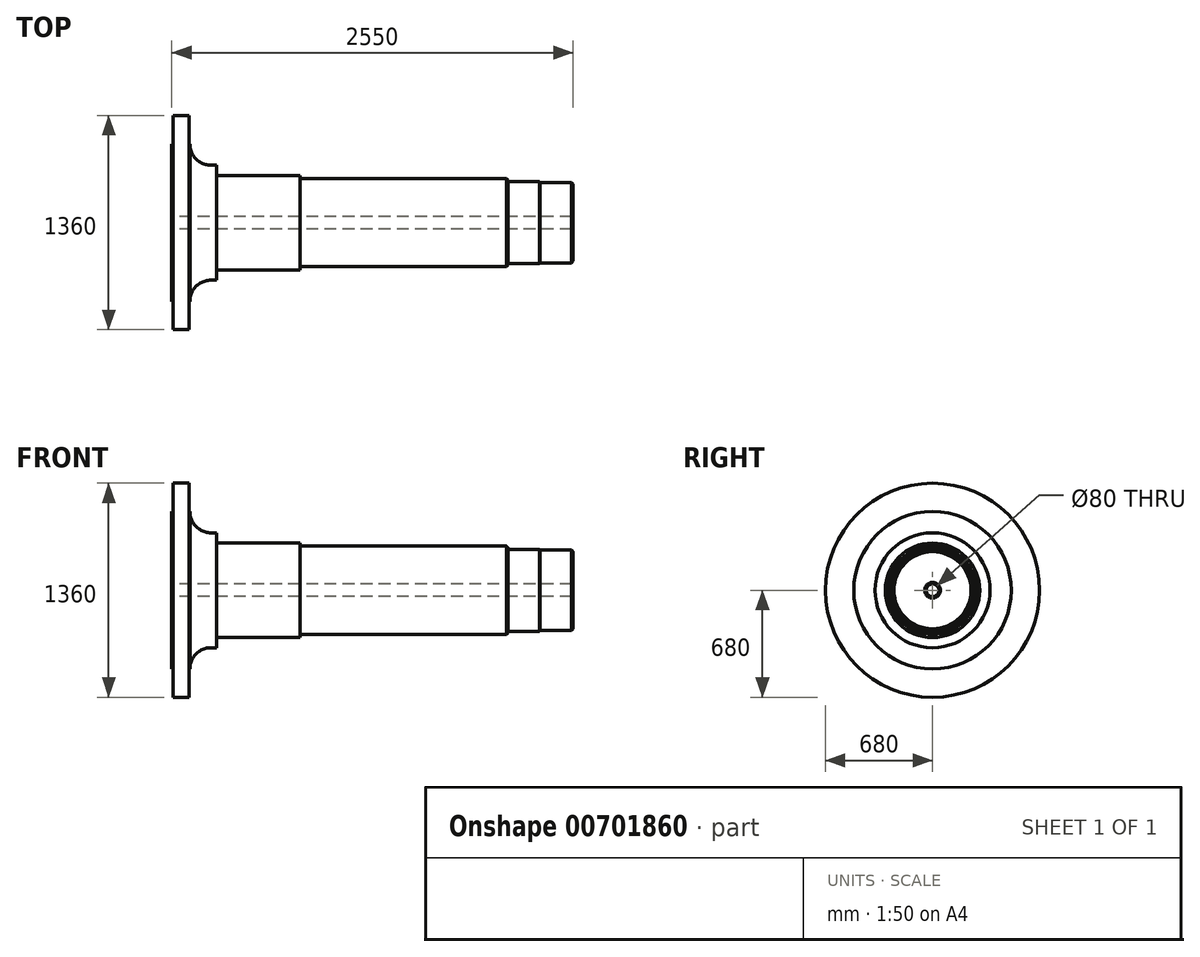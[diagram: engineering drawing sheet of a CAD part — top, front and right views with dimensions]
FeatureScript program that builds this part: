
annotation { "Feature Type Name" : "Feature", "Feature Type Description" : "" }
export const myFeature = defineFeature(function(context is Context, id is Id, definition is map)
    precondition{}
    {
        {
            var Q0;
            Q0=qCreatedBy(makeId("Front.planeOp"),FACE);
            var sketch = newSketch(context, id + "F0", { "sketchPlane" : qUnion([Q0])});
            skLineSegment(sketch, "E0", {"start": v(10, 40) * mm, "end": v(0, 50) * mm});
            skLineSegment(sketch, "E1", {"start": v(0, 50) * mm, "end": v(0, 500) * mm});
            skLineSegment(sketch, "E2", {"start": v(0, 500) * mm, "end": v(10, 500) * mm});
            skLineSegment(sketch, "E3", {"start": v(10, 500) * mm, "end": v(10, 680) * mm});
            skLineSegment(sketch, "E4", {"start": v(10, 680) * mm, "end": v(110, 680) * mm});
            skLineSegment(sketch, "E5", {"start": v(110, 680) * mm, "end": v(110, 500) * mm});
            skLineSegment(sketch, "E6", {"start": v(110, 500) * mm, "end": v(115, 500) * mm});
            skArc(sketch, "E7", {"start": v(115, 500) * mm, "mid": v(154.54, 404.54) * mm, "end": v(250, 365) * mm});
            skLineSegment(sketch, "E8", {"start": v(250, 365) * mm, "end": v(285, 365) * mm});
            skLineSegment(sketch, "E9", {"start": v(285, 365) * mm, "end": v(285, 300) * mm});
            skLineSegment(sketch, "E10", {"start": v(285, 300) * mm, "end": v(815, 300) * mm});
            skLineSegment(sketch, "E11", {"start": v(815, 300) * mm, "end": v(815, 280) * mm});
            skLineSegment(sketch, "E12", {"start": v(2550, 245) * mm, "end": v(2550, 50) * mm});
            skLineSegment(sketch, "E13", {"start": v(2550, 50) * mm, "end": v(2540, 40) * mm});
            skLineSegment(sketch, "E14", {"start": v(2540, 40) * mm, "end": v(10, 40) * mm});
            skLineSegment(sketch, "E15", {"start": v(0, 0) * mm, "end": v(2550, 0) * mm, "construction": true});
            skLineSegment(sketch, "E16", {"start": v(115, 500) * mm, "end": v(115, 505) * mm, "construction": true});
            skLineSegment(sketch, "E17", {"start": v(2135, 260) * mm, "end": v(2335, 260) * mm});
            skLineSegment(sketch, "E18", {"start": v(2335, 260) * mm, "end": v(2340, 255) * mm});
            skLineSegment(sketch, "E19", {"start": v(2340, 255) * mm, "end": v(2540, 255) * mm});
            skLineSegment(sketch, "E20", {"start": v(2550, 245) * mm, "end": v(2540, 255) * mm});
            skLineSegment(sketch, "E21", {"start": v(815, 280) * mm, "end": v(2125, 280) * mm});
            skLineSegment(sketch, "E22", {"start": v(2125, 280) * mm, "end": v(2135, 270) * mm});
            skLineSegment(sketch, "E23", {"start": v(2135, 270) * mm, "end": v(2135, 260) * mm});
            skPoint(sketch, "E24.orphan", {"position": v(815, 260) * mm});
            skSolve(sketch);
        }
        {
            var Q0;
            Q0=qSketchRegion(id+"F0",true);
            var Q1;
            Q1=sQuery(id+"F0.wireOp",EDGE,"E15");
            revolve(context, id + "F1", {"entities" : qUnion([Q0]), "axis" : qUnion([Q1]), "revolveType" : RevolveType.FULL});
        }
    });
